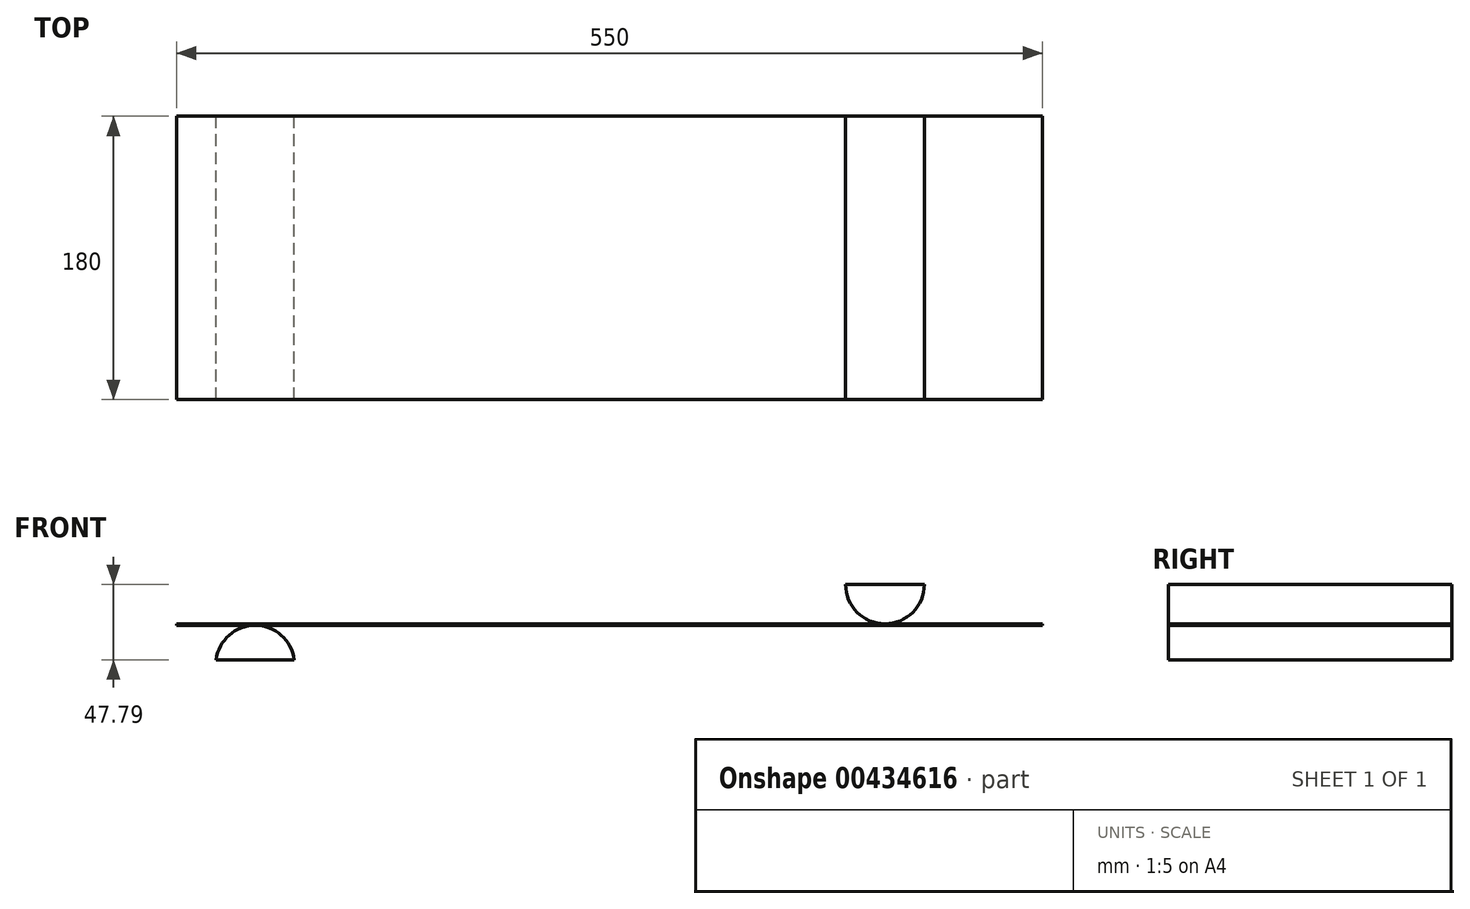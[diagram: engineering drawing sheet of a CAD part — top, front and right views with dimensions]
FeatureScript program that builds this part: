
annotation { "Feature Type Name" : "Feature", "Feature Type Description" : "" }
export const myFeature = defineFeature(function(context is Context, id is Id, definition is map)
    precondition{}
    {
        {
            var Q0;
            Q0=qCreatedBy(makeId("Front.planeOp"),FACE);
            var sketch = newSketch(context, id + "F0", { "sketchPlane" : qUnion([Q0])});
            skLineSegment(sketch, "E0.bottom", {"start": v(12.66, -9.4) * mm, "end": v(562.66, -9.4) * mm});
            skLineSegment(sketch, "E0.top", {"start": v(12.66, -8.4) * mm, "end": v(562.66, -8.4) * mm});
            skLineSegment(sketch, "E0.left", {"start": v(12.66, -9.4) * mm, "end": v(12.66, -8.4) * mm});
            skLineSegment(sketch, "E0.right", {"start": v(562.66, -9.4) * mm, "end": v(562.66, -8.4) * mm});
            skLineSegment(sketch, "E1", {"start": v(37.87, -31.2) * mm, "end": v(87.46, -31.2) * mm});
            skArc(sketch, "E2", {"start": v(87.46, -31.2) * mm, "mid": v(62.66, -9.4) * mm, "end": v(37.87, -31.2) * mm});
            skLineSegment(sketch, "E3", {"start": v(437.66, 16.6) * mm, "end": v(487.66, 16.6) * mm});
            skArc(sketch, "E4", {"start": v(437.66, 16.6) * mm, "mid": v(462.66, -8.4) * mm, "end": v(487.66, 16.6) * mm});
            skSolve(sketch);
        }
        {
            var Q0;
            {var subQ0=sQuery(id+"F0.wireOp",EDGE,"E3");Q0=makeQuery(id+"F0.imprint","IMPRINT",FACE,{"disambiguationData":[TD([[makeQuery(id+"F0.imprint","IMPRINT",EDGE,{"derivedFrom":subQ0}),-1.0]])]});}
            var Q1;
            {var subQ3=sQuery(id+"F0.wireOp",EDGE,"E0.left");Q1=makeQuery(id+"F0.imprint","IMPRINT",FACE,{"disambiguationData":[TD([[makeQuery(id+"F0.imprint","IMPRINT",EDGE,{"derivedFrom":subQ3}),-1.0]])]});}
            var Q2;
            {var subQ0=sQuery(id+"F0.wireOp",EDGE,"E1");Q2=makeQuery(id+"F0.imprint","IMPRINT",FACE,{"disambiguationData":[TD([[makeQuery(id+"F0.imprint","IMPRINT",EDGE,{"derivedFrom":subQ0}),1.0]])]});}
            extrude(context, id + "F1", {"entities" : qUnion([Q0, Q1, Q2]), "depth" : 180 * mm});
        }
    });
